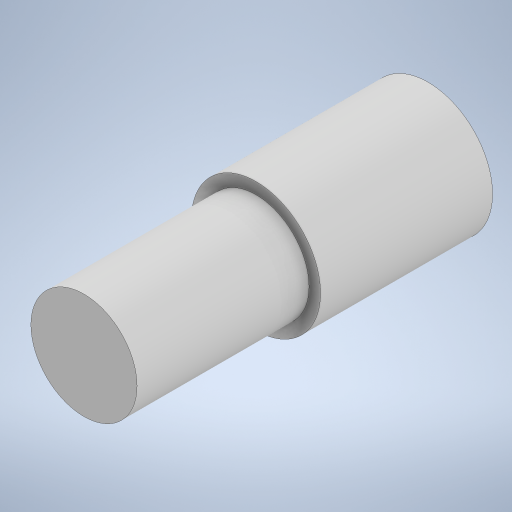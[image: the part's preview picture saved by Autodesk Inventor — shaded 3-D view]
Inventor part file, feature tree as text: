
AUTODESK INVENTOR PART (.ipt)
format: ipt  version: 2023.1 (Build 271208000, 208)  size: 222,720 bytes
history: native  units: mm
features: extrude x2, other x1, sketch x1
ambient origin geometry x8: Origin, YZ Plane, XZ Plane, XY Plane, X Axis, Y Axis, Z Axis, Center Point
bodies: Body1 (feature_tree)
feature tree (4):
  other  "솔리드1"
  sketch  "스케치1"
  extrude  "돌출1"  Depth=22.5mm
  extrude  "돌출2"  Depth=18.5mm
